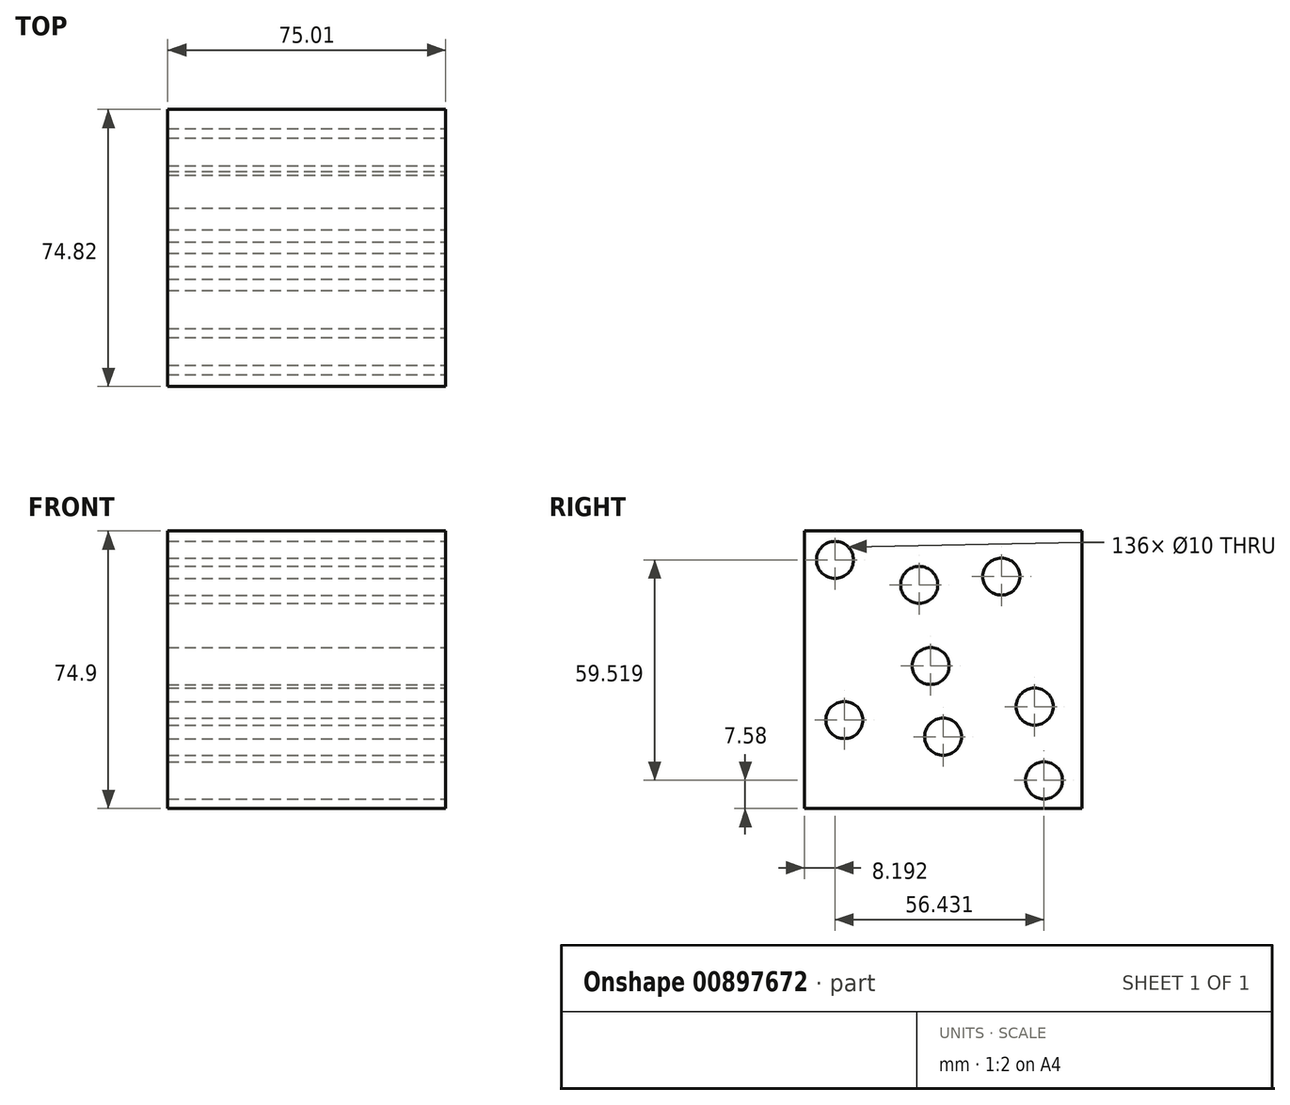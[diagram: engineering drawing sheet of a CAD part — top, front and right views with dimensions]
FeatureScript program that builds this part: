
annotation { "Feature Type Name" : "Feature", "Feature Type Description" : "" }
export const myFeature = defineFeature(function(context is Context, id is Id, definition is map)
    precondition{}
    {
        {
            var Q0;
            Q0=qCreatedBy(makeId("Top.planeOp"),FACE);
            var sketch = newSketch(context, id + "F0", { "sketchPlane" : qUnion([Q0])});
            skLineSegment(sketch, "E0.bottom", {"start": v(0, 0) * mm, "end": v(75.01, 0) * mm});
            skLineSegment(sketch, "E0.top", {"start": v(0, -74.82) * mm, "end": v(75.01, -74.82) * mm});
            skLineSegment(sketch, "E0.left", {"start": v(0, 0) * mm, "end": v(0, -74.82) * mm});
            skLineSegment(sketch, "E0.right", {"start": v(75.01, 0) * mm, "end": v(75.01, -74.82) * mm});
            skSolve(sketch);
        }
        {
            var Q0;
            Q0=makeQuery(id+"F0.imprint","IMPRINT",FACE,{"disambiguationData":[TD([[makeQuery(id+"F0.imprint","IMPRINT",EDGE,{"derivedFrom":sQuery(id+"F0.wireOp",EDGE,"E0.bottom")}),-1.0]])]});
            extrude(context, id + "F1", {"entities" : qUnion([Q0]), "depth" : 74.9 * mm, "offsetDistance" : 25 * mm});
        }
        {
            var Q0;
            Q0=makeQuery(id+"F1.opExtrude","SWEPT_FACE",FACE,{"disambiguationData":[OSD([sQuery(id+"F0.wireOp",EDGE,"E0.right")])]});
            var sketch = newSketch(context, id + "F2", { "sketchPlane" : qUnion([Q0])});
            skCircle(sketch, "E1", {"center": v(-66.63, 67.1) * mm, "radius": 6.58 * mm});
            skCircle(sketch, "E2", {"center": v(-40.8, 38.46) * mm, "radius": 13.92 * mm});
            skCircle(sketch, "E3", {"center": v(-21.7, 62.6) * mm, "radius": 5.45 * mm});
            skCircle(sketch, "E4", {"center": v(-12.72, 27.51) * mm, "radius": 4.44 * mm});
            skCircle(sketch, "E5", {"center": v(-37.43, 19.37) * mm, "radius": 11.18 * mm});
            skCircle(sketch, "E6", {"center": v(-64.1, 23.86) * mm, "radius": 6.16 * mm});
            skCircle(sketch, "E7", {"center": v(-10.2, 7.58) * mm, "radius": 5.27 * mm});
            skCircle(sketch, "E8", {"center": v(-43.89, 60.36) * mm, "radius": 4.53 * mm});
            skSolve(sketch);
        }
        {
            var Q0;
            Q0=sQuery(id+"F2.wireOp",VERTEX,"E3.center");
            var Q1;
            Q1=sQuery(id+"F2.wireOp",VERTEX,"E2.center");
            var Q2;
            Q2=sQuery(id+"F2.wireOp",VERTEX,"E5.center");
            var Q3;
            Q3=sQuery(id+"F2.wireOp",VERTEX,"E1.center");
            var Q4;
            Q4=sQuery(id+"F2.wireOp",VERTEX,"E8.center");
            var Q5;
            Q5=sQuery(id+"F2.wireOp",VERTEX,"E4.center");
            var Q6;
            Q6=sQuery(id+"F2.wireOp",VERTEX,"E6.center");
            var Q7;
            Q7=sQuery(id+"F2.wireOp",VERTEX,"E7.center");
            var Q8;
            Q8=makeQuery(id+"F1.opExtrude","SWEPT_BODY",BODY,{"disambiguationData":[OSD([sQuery(id+"F0.wireOp",EDGE,"E0.bottom"),sQuery(id+"F0.wireOp",EDGE,"E0.top"),sQuery(id+"F0.wireOp",EDGE,"E0.left"),sQuery(id+"F0.wireOp",EDGE,"E0.right")])]});
            hole(context, id + "F3", {"style" : HoleStyle.SIMPLE, "endStyle" : HoleEndStyle.THROUGH, "holeDiameter" : 10 * mm, "majorDiameter" : 5 * mm, "isTappedThrough" : true, "tappedDepth" : 12 * mm, "tapClearance" : 3, "locations" : qUnion([Q0, Q1, Q2, Q3, Q4, Q5, Q6, Q7]), "scope" : qUnion([Q8])});
        }
    });
